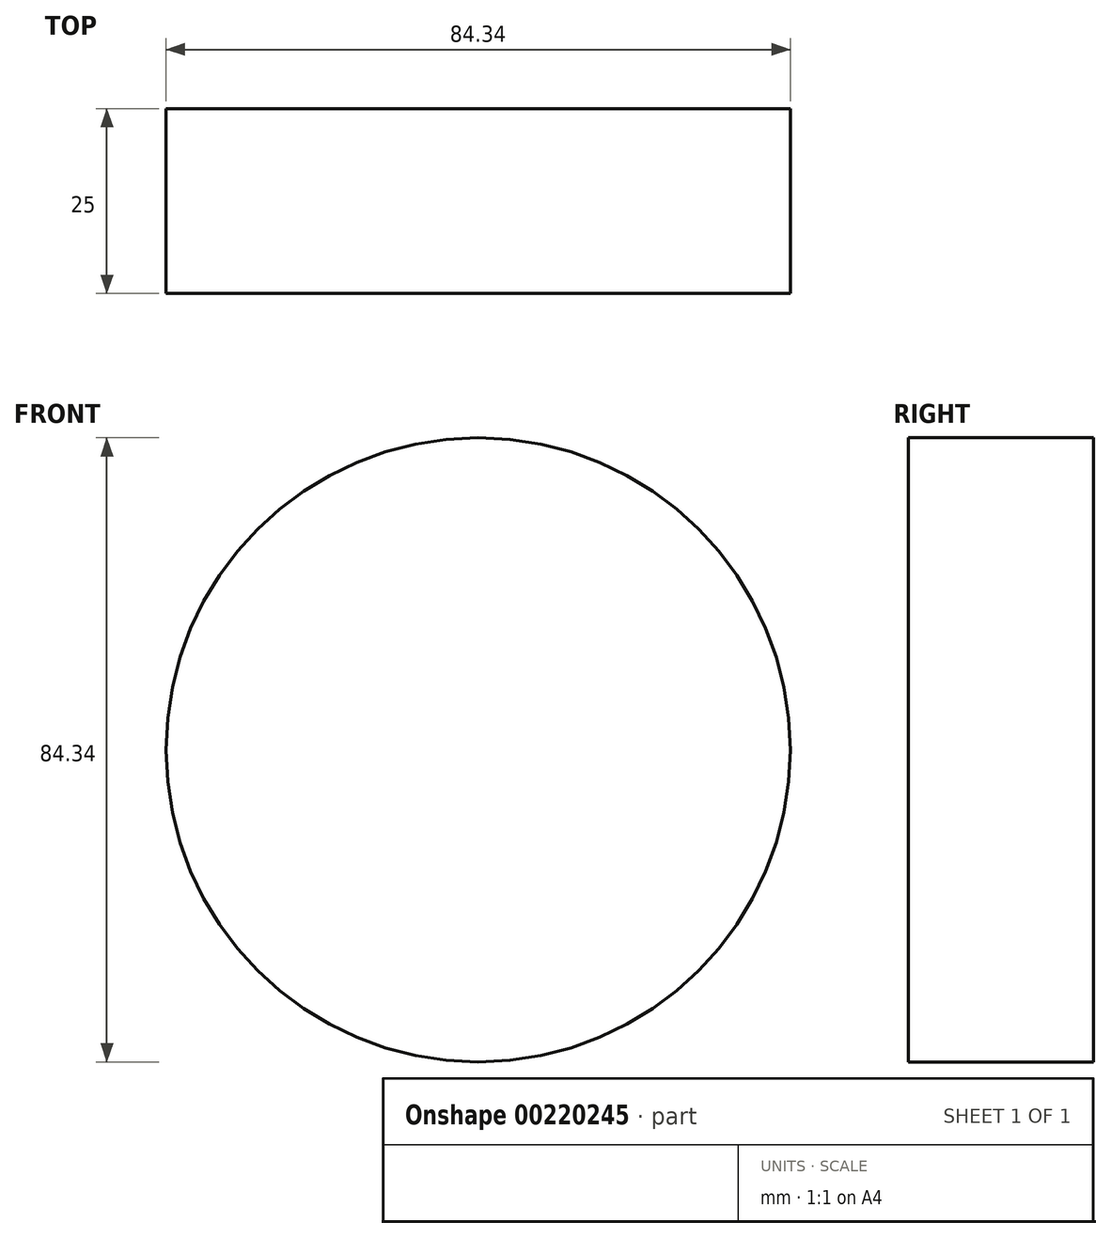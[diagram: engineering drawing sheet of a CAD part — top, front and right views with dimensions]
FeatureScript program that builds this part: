
annotation { "Feature Type Name" : "Feature", "Feature Type Description" : "" }
export const myFeature = defineFeature(function(context is Context, id is Id, definition is map)
    precondition{}
    {
        {
            var Q0;
            Q0=qCreatedBy(makeId("Front.planeOp"),FACE);
            var sketch = newSketch(context, id + "F0", { "sketchPlane" : qUnion([Q0])});
            skCircle(sketch, "E0", {"center": v(0, 0) * mm, "radius": 42.17 * mm});
            skSolve(sketch);
        }
        {
            var Q0;
            Q0=makeQuery(id+"F0.imprint","IMPRINT",FACE,{"disambiguationData":[TD([[makeQuery(id+"F0.imprint","IMPRINT",EDGE,{"derivedFrom":sQuery(id+"F0.wireOp",EDGE,"E0")}),1.0]])]});
            extrude(context, id + "F1", {"entities" : qUnion([Q0]), "depth" : 25 * mm});
        }
    });
